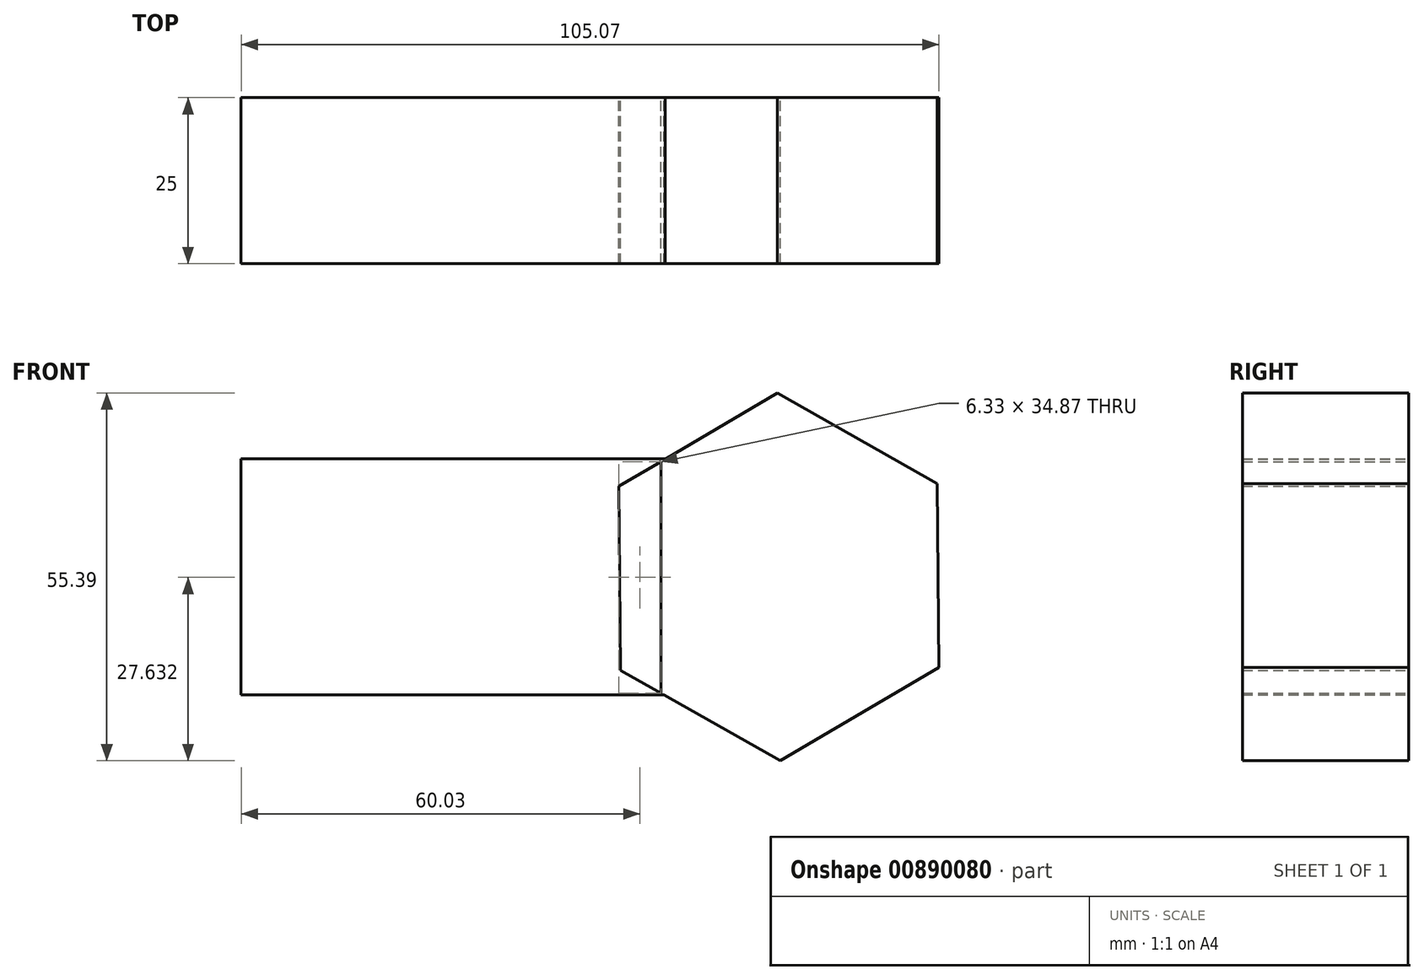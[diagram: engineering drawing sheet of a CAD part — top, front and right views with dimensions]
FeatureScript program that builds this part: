
annotation { "Feature Type Name" : "Feature", "Feature Type Description" : "" }
export const myFeature = defineFeature(function(context is Context, id is Id, definition is map)
    precondition{}
    {
        {
            var Q0;
            Q0=qCreatedBy(makeId("Front.planeOp"),FACE);
            var sketch = newSketch(context, id + "F0", { "sketchPlane" : qUnion([Q0])});
            skLineSegment(sketch, "E0.bottom", {"start": v(-92.78, 21.12) * mm, "end": v(-29.58, 21.12) * mm});
            skLineSegment(sketch, "E0.top", {"start": v(-92.78, -14.42) * mm, "end": v(-29.58, -14.42) * mm});
            skLineSegment(sketch, "E0.left", {"start": v(-92.78, 21.12) * mm, "end": v(-92.78, -14.42) * mm});
            skLineSegment(sketch, "E0.right", {"start": v(-29.58, 21.12) * mm, "end": v(-29.58, -14.42) * mm});
            skArc(sketch, "E1", {"start": v(-29.58, -14.42) * mm, "mid": v(-11.81, 3.35) * mm, "end": v(-29.58, 21.12) * mm});
            skCircle(sketch, "E2.cCircle", {"center": v(-11.81, 3.35) * mm, "radius": 23.99 * mm, "construction": true});
            skLineSegment(sketch, "E2.0", {"start": v(-12.05, 31.04) * mm, "end": v(12.05, 17.4) * mm});
            skLineSegment(sketch, "E2.1", {"start": v(12.05, 17.4) * mm, "end": v(12.3, -10.3) * mm});
            skLineSegment(sketch, "E2.2", {"start": v(12.3, -10.3) * mm, "end": v(-11.57, -24.35) * mm});
            skLineSegment(sketch, "E2.3", {"start": v(-11.57, -24.35) * mm, "end": v(-35.68, -10.7) * mm});
            skLineSegment(sketch, "E2.4", {"start": v(-35.68, -10.7) * mm, "end": v(-35.92, 16.99) * mm});
            skLineSegment(sketch, "E2.5", {"start": v(-35.92, 16.99) * mm, "end": v(-12.05, 31.04) * mm});
            skPoint(sketch, "E2.0.midPoint", {"position": v(0, 24.22) * mm});
            skSolve(sketch);
        }
        {
            var Q0;
            {var subQ2=sQuery(id+"F0.wireOp",EDGE,"E0.bottom");Q0=makeQuery(id+"F0.imprint","IMPRINT",FACE,{"disambiguationData":[TD([[makeQuery(id+"F0.imprint","IMPRINT",EDGE,{"derivedFrom":subQ2}),-1.0]])]});}
            var Q1;
            {var subQ1=sQuery(id+"F0.wireOp",EDGE,"E2.0");Q1=makeQuery(id+"F0.imprint","IMPRINT",FACE,{"disambiguationData":[TD([[makeQuery(id+"F0.imprint","IMPRINT",EDGE,{"derivedFrom":subQ1}),-1.0]])]});}
            var Q2;
            {var subQ0=sQuery(id+"F0.wireOp",EDGE,"E1");var subQ3=sQuery(id+"F0.wireOp",EDGE,"E2.5");var subQ5=makeQuery(id+"F0.imprint","INTERSECT",VERTEX,{"derivedFrom":[subQ0,subQ3]});Q2=makeQuery(id+"F0.imprint","IMPRINT",FACE,{"disambiguationData":[TD([[makeQuery(id+"F0.imprint","IMPRINT",EDGE,{"disambiguationData":[TD([[subQ5,1.0]])],"derivedFrom":subQ3}),1.0]])]});}
            var Q3;
            {var subQ0=sQuery(id+"F0.wireOp",EDGE,"E1");var subQ3=sQuery(id+"F0.wireOp",EDGE,"E2.3");var subQ5=makeQuery(id+"F0.imprint","INTERSECT",VERTEX,{"derivedFrom":[subQ0,subQ3]});Q3=makeQuery(id+"F0.imprint","IMPRINT",FACE,{"disambiguationData":[TD([[makeQuery(id+"F0.imprint","IMPRINT",EDGE,{"disambiguationData":[TD([[subQ5,-1.0]])],"derivedFrom":subQ3}),1.0]])]});}
            var Q4;
            {var subQ0=sQuery(id+"F0.wireOp",EDGE,"E2.5");var subQ1=sQuery(id+"F0.wireOp",EDGE,"E0.right");var subQ2=makeQuery(id+"F0.imprint","INTERSECT",VERTEX,{"derivedFrom":[subQ1,subQ0]});Q4=makeQuery(id+"F0.imprint","IMPRINT",FACE,{"disambiguationData":[TD([[makeQuery(id+"F0.imprint","IMPRINT",EDGE,{"disambiguationData":[TD([[subQ2,-1.0]])],"derivedFrom":subQ1}),1.0]])]});}
            extrude(context, id + "F1", {"entities" : qUnion([Q0, Q1, Q2, Q3, Q4]), "depth" : 25 * mm, "offsetDistance" : 25 * mm});
        }
    });
